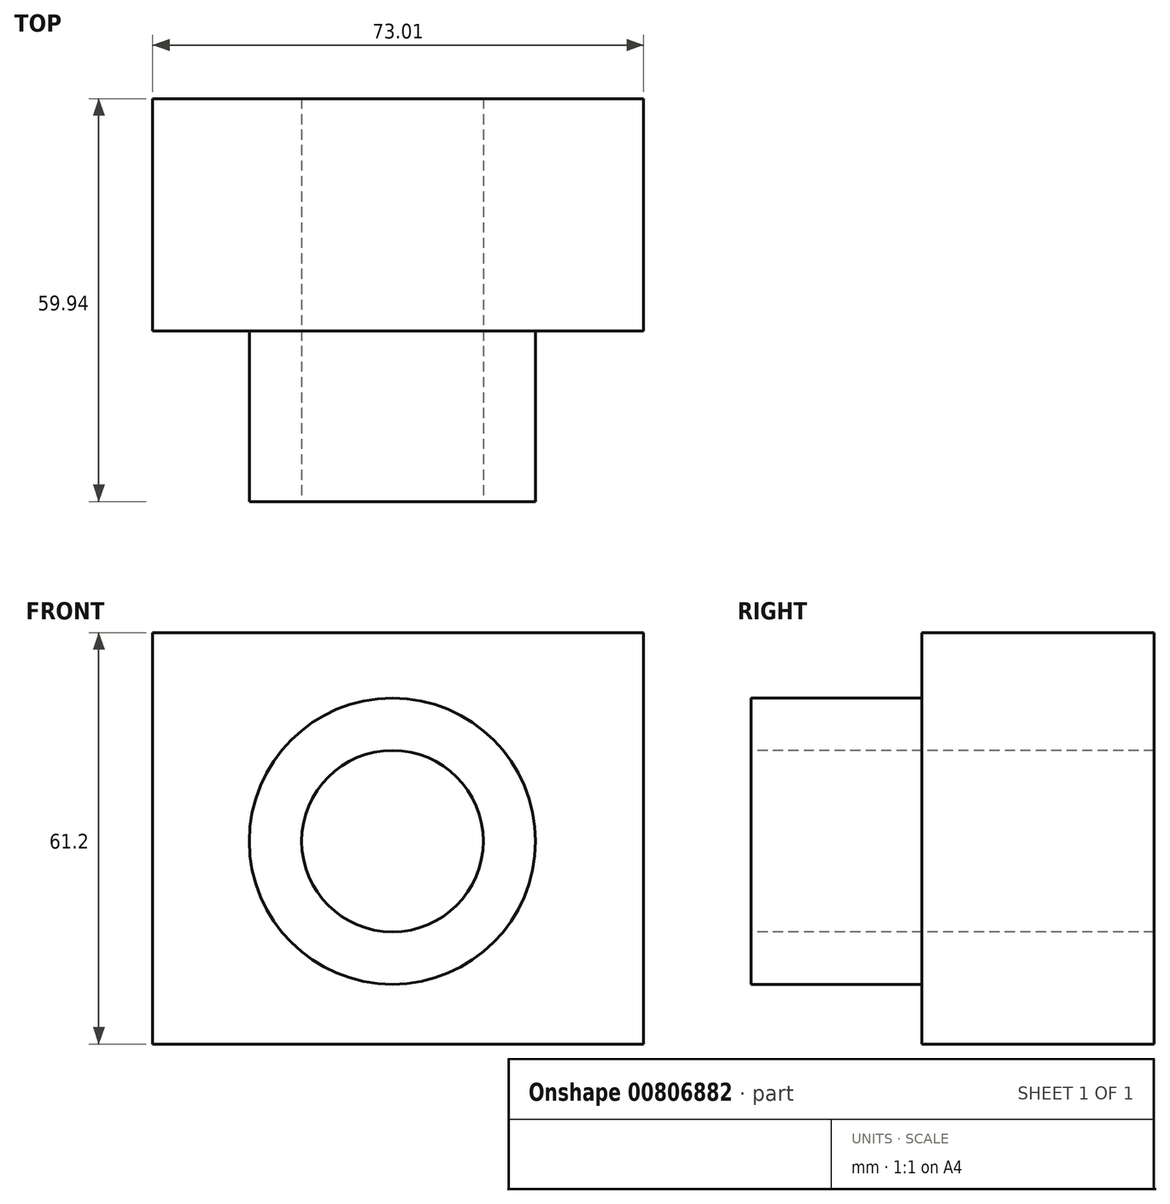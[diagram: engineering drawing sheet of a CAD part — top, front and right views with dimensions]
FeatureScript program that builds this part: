
annotation { "Feature Type Name" : "Feature", "Feature Type Description" : "" }
export const myFeature = defineFeature(function(context is Context, id is Id, definition is map)
    precondition{}
    {
        {
            var Q0;
            Q0=qCreatedBy(makeId("Front.planeOp"),FACE);
            var sketch = newSketch(context, id + "F0", { "sketchPlane" : qUnion([Q0])});
            skLineSegment(sketch, "E0.bottom", {"start": v(-51.86, 21.82) * mm, "end": v(21.15, 21.82) * mm});
            skLineSegment(sketch, "E0.top", {"start": v(-51.86, -39.38) * mm, "end": v(21.15, -39.38) * mm});
            skLineSegment(sketch, "E0.left", {"start": v(-51.86, 21.82) * mm, "end": v(-51.86, -39.38) * mm});
            skLineSegment(sketch, "E0.right", {"start": v(21.15, 21.82) * mm, "end": v(21.15, -39.38) * mm});
            skSolve(sketch);
        }
        {
            var Q0;
            Q0 = qSketchRegion(id + "F0", true);
            extrude(context, id + "F1", {"entities" : qUnion([Q0]), "oppositeDirection" : true, "depth" : 34.54 * mm, "offsetDistance" : 25.4 * mm});
        }
        {
            var Q0;
            Q0=makeQuery(id+"F1.opExtrude","CAP_FACE",FACE,{"disambiguationData":[OSD([sQuery(id+"F0.wireOp",EDGE,"E0.bottom"),sQuery(id+"F0.wireOp",EDGE,"E0.top"),sQuery(id+"F0.wireOp",EDGE,"E0.left"),sQuery(id+"F0.wireOp",EDGE,"E0.right")])],"isStart":true});
            var sketch = newSketch(context, id + "F2", { "sketchPlane" : qUnion([Q0])});
            skCircle(sketch, "E1", {"center": v(-16.2, -9.2) * mm, "radius": 21.29 * mm});
            skCircle(sketch, "E2", {"center": v(-16.2, -9.2) * mm, "radius": 13.5 * mm});
            skSolve(sketch);
        }
        {
            var Q0;
            Q0=makeQuery(id+"F2.imprint","IMPRINT",FACE,{"disambiguationData":[TD([[makeQuery(id+"F2.imprint","IMPRINT",EDGE,{"derivedFrom":sQuery(id+"F2.wireOp",EDGE,"E2")}),1.0]])]});
            extrude(context, id + "F3", {"entities" : qUnion([Q0]), "operationType" : NewBodyOperationType.REMOVE, "oppositeDirection" : true, "depth" : 69.34 * mm, "offsetDistance" : 25.4 * mm});
        }
        {
            var Q0;
            Q0 = qSketchRegion(id + "F2", true);
            extrude(context, id + "F4", {"entities" : qUnion([Q0]), "operationType" : NewBodyOperationType.ADD, "depth" : 25.4 * mm, "offsetDistance" : 25.4 * mm});
        }
    });
